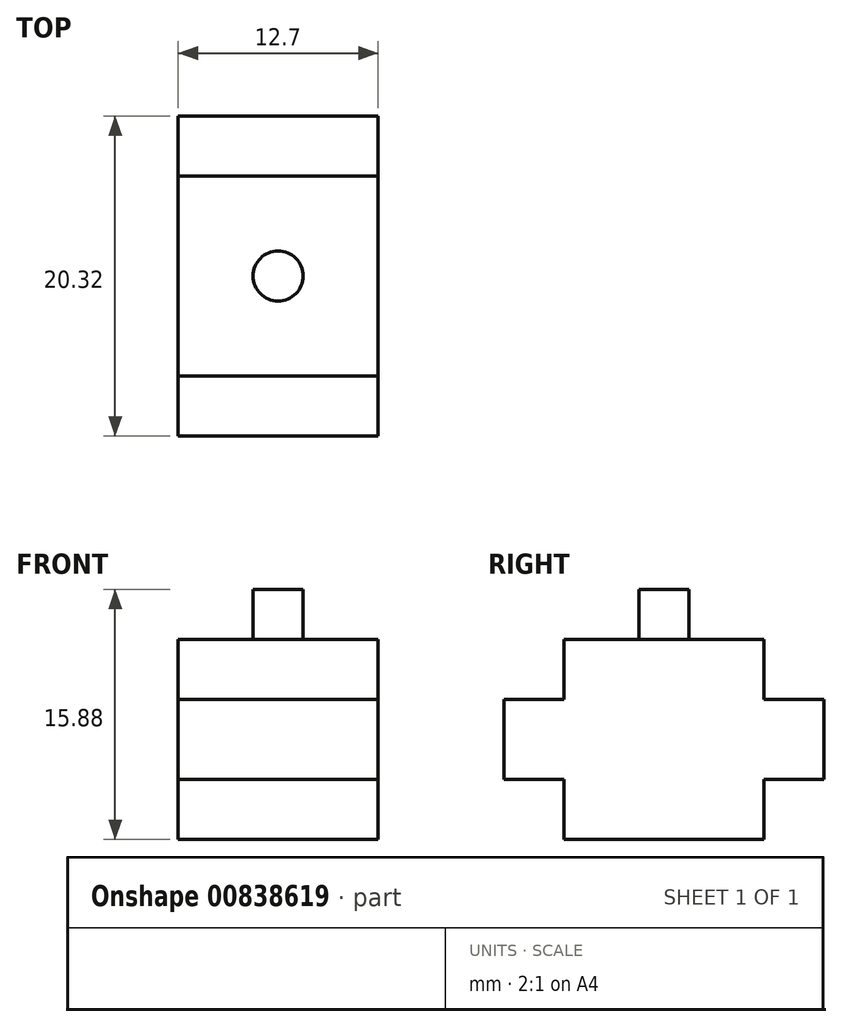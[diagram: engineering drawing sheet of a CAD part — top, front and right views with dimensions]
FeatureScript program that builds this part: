
annotation { "Feature Type Name" : "Feature", "Feature Type Description" : "" }
export const myFeature = defineFeature(function(context is Context, id is Id, definition is map)
    precondition{}
    {
        {
            var Q0;
            Q0=qCreatedBy(makeId("Top.planeOp"),FACE);
            var sketch = newSketch(context, id + "F0", { "sketchPlane" : qUnion([Q0])});
            skLineSegment(sketch, "E0.bottom", {"start": v(0, 0) * mm, "end": v(12.7, 0) * mm});
            skLineSegment(sketch, "E0.top", {"start": v(0, 12.7) * mm, "end": v(12.7, 12.7) * mm});
            skLineSegment(sketch, "E0.left", {"start": v(0, 0) * mm, "end": v(0, 12.7) * mm});
            skLineSegment(sketch, "E0.right", {"start": v(12.7, 0) * mm, "end": v(12.7, 12.7) * mm});
            skSolve(sketch);
        }
        {
            var Q0;
            Q0=makeQuery(id+"F0.imprint","IMPRINT",FACE,{"disambiguationData":[TD([[makeQuery(id+"F0.imprint","IMPRINT",EDGE,{"derivedFrom":sQuery(id+"F0.wireOp",EDGE,"E0.bottom")}),1.0]])]});
            extrude(context, id + "F1", {"entities" : qUnion([Q0]), "depth" : 12.7 * mm, "offsetDistance" : 25.4 * mm});
        }
        {
            var Q0;
            Q0=makeQuery(id+"F1.opExtrude","CAP_FACE",FACE,{"disambiguationData":[OSD([sQuery(id+"F0.wireOp",EDGE,"E0.bottom"),sQuery(id+"F0.wireOp",EDGE,"E0.top"),sQuery(id+"F0.wireOp",EDGE,"E0.left"),sQuery(id+"F0.wireOp",EDGE,"E0.right")])],"isStart":false});
            var sketch = newSketch(context, id + "F2", { "sketchPlane" : qUnion([Q0])});
            skCircle(sketch, "E1", {"center": v(6.35, 6.35) * mm, "radius": 1.59 * mm});
            skSolve(sketch);
        }
        {
            var Q0;
            Q0=makeQuery(id+"F2.imprint","IMPRINT",FACE,{"disambiguationData":[TD([[makeQuery(id+"F2.imprint","IMPRINT",EDGE,{"derivedFrom":sQuery(id+"F2.wireOp",EDGE,"E1")}),1.0]])]});
            extrude(context, id + "F3", {"entities" : qUnion([Q0]), "operationType" : NewBodyOperationType.ADD, "depth" : 3.17 * mm, "offsetDistance" : 25.4 * mm});
        }
        {
            var Q0;
            Q0=makeQuery(id+"F1.opExtrude","SWEPT_FACE",FACE,{"disambiguationData":[OSD([sQuery(id+"F0.wireOp",EDGE,"E0.bottom")])]});
            var sketch = newSketch(context, id + "F4", { "sketchPlane" : qUnion([Q0])});
            skLineSegment(sketch, "E2.bottom", {"start": v(0, 3.8) * mm, "end": v(12.7, 3.8) * mm});
            skLineSegment(sketch, "E2.top", {"start": v(0, 8.9) * mm, "end": v(12.7, 8.9) * mm});
            skLineSegment(sketch, "E2.left", {"start": v(0, 3.8) * mm, "end": v(0, 8.9) * mm});
            skLineSegment(sketch, "E2.right", {"start": v(12.7, 3.81) * mm, "end": v(12.7, 8.9) * mm});
            skSolve(sketch);
        }
        {
            var Q0;
            Q0=makeQuery(id+"F4.imprint","IMPRINT",FACE,{"disambiguationData":[TD([[makeQuery(id+"F4.imprint","IMPRINT",EDGE,{"derivedFrom":sQuery(id+"F4.wireOp",EDGE,"E2.bottom")}),1.0]])]});
            extrude(context, id + "F5", {"entities" : qUnion([Q0]), "operationType" : NewBodyOperationType.ADD, "depth" : 3.8 * mm, "offsetDistance" : 25.4 * mm});
        }
        {
            var Q0;
            Q0=makeQuery(id+"F1.opExtrude","SWEPT_FACE",FACE,{"disambiguationData":[OSD([sQuery(id+"F0.wireOp",EDGE,"E0.top")])]});
            var sketch = newSketch(context, id + "F6", { "sketchPlane" : qUnion([Q0])});
            skLineSegment(sketch, "E3.bottom", {"start": v(-12.7, 3.8) * mm, "end": v(0, 3.8) * mm});
            skLineSegment(sketch, "E3.top", {"start": v(-12.7, 8.9) * mm, "end": v(0, 8.9) * mm});
            skLineSegment(sketch, "E3.left", {"start": v(-12.7, 3.8) * mm, "end": v(-12.7, 8.9) * mm});
            skLineSegment(sketch, "E3.right", {"start": v(0, 3.8) * mm, "end": v(0, 8.9) * mm});
            skSolve(sketch);
        }
        {
            var Q0;
            Q0=makeQuery(id+"F6.imprint","IMPRINT",FACE,{"disambiguationData":[TD([[makeQuery(id+"F6.imprint","IMPRINT",EDGE,{"derivedFrom":sQuery(id+"F6.wireOp",EDGE,"E3.bottom")}),1.0]])]});
            extrude(context, id + "F7", {"entities" : qUnion([Q0]), "operationType" : NewBodyOperationType.ADD, "depth" : 3.8 * mm, "offsetDistance" : 25.4 * mm});
        }
    });
